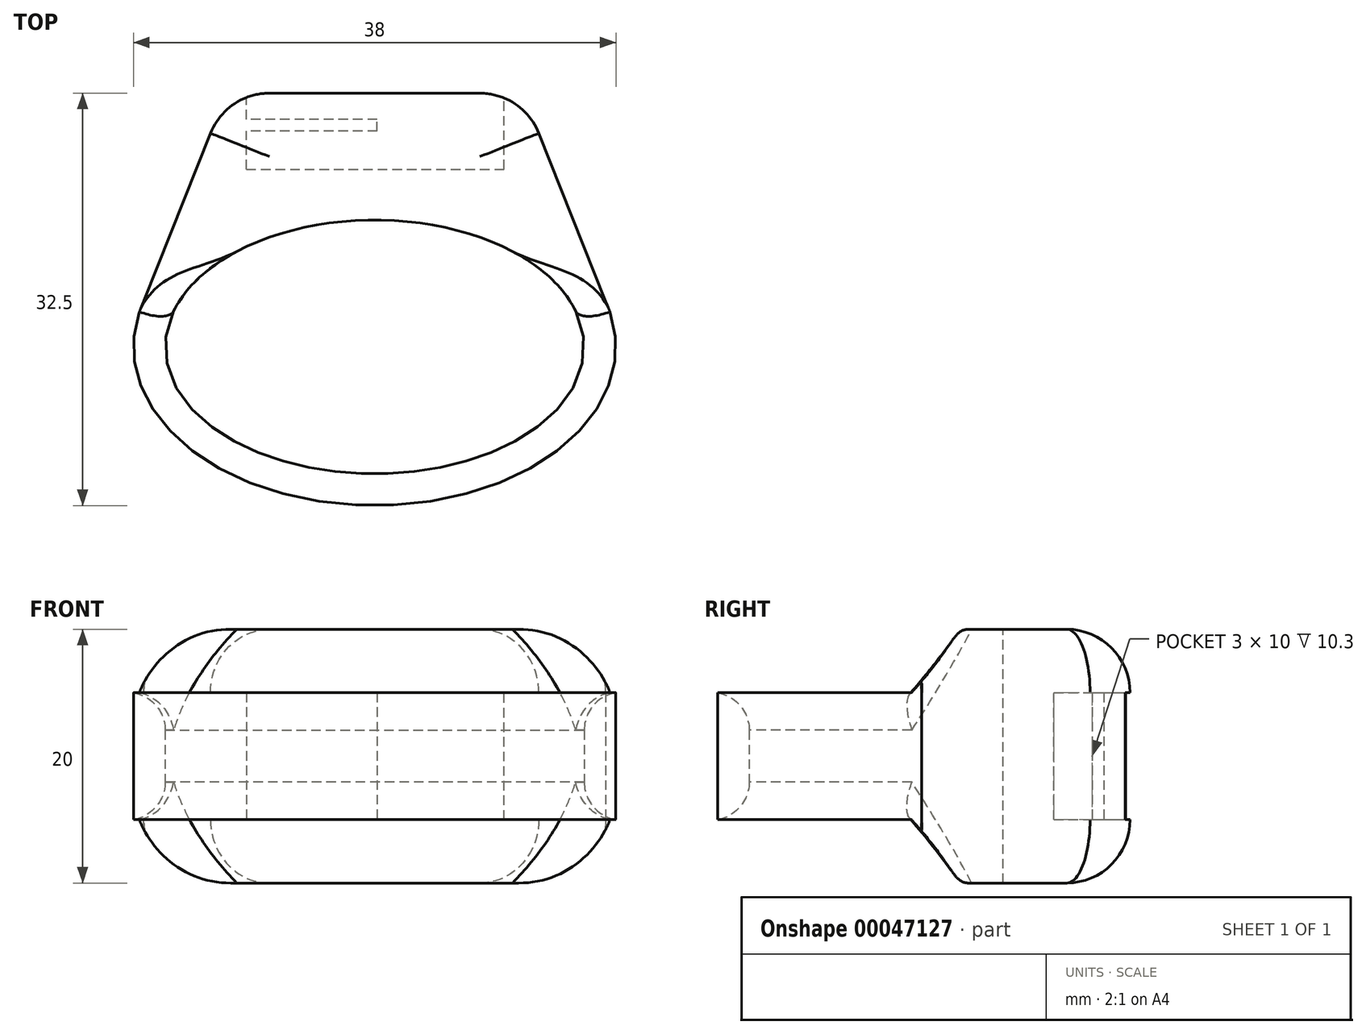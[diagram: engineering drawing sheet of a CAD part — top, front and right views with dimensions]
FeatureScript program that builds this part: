
annotation { "Feature Type Name" : "Feature", "Feature Type Description" : "" }
export const myFeature = defineFeature(function(context is Context, id is Id, definition is map)
    precondition{}
    {
        {
            var Q0;
            Q0=qCreatedBy(makeId("Top.planeOp"),FACE);
            var sketch = newSketch(context, id + "F0", { "sketchPlane" : qUnion([Q0])});
            skEllipse(sketch, "E0", {"center": v(0, 0) * mm, "majorRadius": 16.5 * mm, "minorRadius": 10 * mm, "majorAxis": v(1, 0)});
            skEllipse(sketch, "E1", {"center": v(0, 0) * mm, "majorRadius": 19 * mm, "minorRadius": 12.5 * mm, "majorAxis": v(1, 0)});
            skPoint(sketch, "E2.endSnap0", {"position": v(0, 12.5) * mm});
            skLineSegment(sketch, "E3", {"start": v(0, 12.5) * mm, "end": v(0, 27.8) * mm, "construction": true});
            skLineSegment(sketch, "E4", {"start": v(11.67, 20) * mm, "end": v(0, 20) * mm});
            skLineSegment(sketch, "E5.MirrorCS", {"start": v(-11.67, 20) * mm, "end": v(0, 20) * mm});
            skLineSegment(sketch, "E6", {"start": v(0, 10) * mm, "end": v(45.24, 10) * mm, "construction": true});
            skPoint(sketch, "E7.end.orphan", {"position": v(18.92, -1.17) * mm});
            skPoint(sketch, "E8.orphan", {"position": v(-18.92, -1.17) * mm});
            skPoint(sketch, "E9.MirrorCS.start.orphan", {"position": v(-11.67, 20) * mm});
            skLineSegment(sketch, "E10", {"start": v(11.67, 20) * mm, "end": v(18.54, 2.73) * mm});
            skLineSegment(sketch, "E11.MirrorCS", {"start": v(-11.67, 20) * mm, "end": v(-18.54, 2.73) * mm});
            skLineSegment(sketch, "E12", {"start": v(-18.54, 2.73) * mm, "end": v(-16.23, 1.81) * mm});
            skLineSegment(sketch, "E13", {"start": v(18.54, 2.73) * mm, "end": v(16.23, 1.81) * mm});
            skSolve(sketch);
        }
        {
            var Q0;
            {var subQ0=sQuery(id+"F0.wireOp",EDGE,"E10");var subQ1=sQuery(id+"F0.wireOp",EDGE,"E1");var subQ3=makeQuery(id+"F0.imprint","INTERSECT",VERTEX,{"derivedFrom":[subQ1,subQ0]});Q0=makeQuery(id+"F0.imprint","IMPRINT",FACE,{"disambiguationData":[TD([[makeQuery(id+"F0.imprint","IMPRINT",EDGE,{"disambiguationData":[TD([[subQ3,1.0]])],"derivedFrom":subQ1}),1.0]])]});}
            var Q1;
            {var subQ2=sQuery(id+"F0.wireOp",EDGE,"E4");Q1=makeQuery(id+"F0.imprint","IMPRINT",FACE,{"disambiguationData":[TD([[makeQuery(id+"F0.imprint","IMPRINT",EDGE,{"derivedFrom":subQ2}),1.0]])]});}
            var Q2;
            {var subQ0=sQuery(id+"F0.wireOp",EDGE,"E11.MirrorCS");var subQ1=sQuery(id+"F0.wireOp",EDGE,"E1");var subQ3=makeQuery(id+"F0.imprint","INTERSECT",VERTEX,{"derivedFrom":[subQ1,subQ0]});Q2=makeQuery(id+"F0.imprint","IMPRINT",FACE,{"disambiguationData":[TD([[makeQuery(id+"F0.imprint","IMPRINT",EDGE,{"disambiguationData":[TD([[subQ3,-1.0]])],"derivedFrom":subQ1}),1.0]])]});}
            var Q3;
            {var subQ0=sQuery(id+"F0.wireOp",EDGE,"E12");Q3=makeQuery(id+"F0.imprint","IMPRINT",FACE,{"disambiguationData":[TD([[makeQuery(id+"F0.imprint","IMPRINT",EDGE,{"derivedFrom":subQ0}),1.0]])]});}
            extrude(context, id + "F1", {"entities" : qUnion([Q0, Q1, Q2, Q3]), "endBound" : BoundingType.SYMMETRIC, "depth" : 20 * mm});
        }
        {
            var Q0;
            Q0 = qSketchRegion(id + "F0", true);
            extrude(context, id + "F2", {"entities" : qUnion([Q0]), "operationType" : NewBodyOperationType.ADD, "endBound" : BoundingType.SYMMETRIC, "depth" : 10 * mm});
        }
        {
            var Q0;
            Q0=makeQuery(id+"F1.opExtrude","CAP_EDGE",EDGE,{"disambiguationData":[OSD([sQuery(id+"F0.wireOp",EDGE,"E12")])],"isStart":true});
            var Q1;
            Q1=makeQuery(id+"F1.opExtrude","CAP_EDGE",EDGE,{"disambiguationData":[OSD([sQuery(id+"F0.wireOp",EDGE,"E12")])],"isStart":false});
            var Q2;
            Q2=makeQuery(id+"F1.opExtrude","CAP_EDGE",EDGE,{"disambiguationData":[OSD([sQuery(id+"F0.wireOp",EDGE,"E13")])],"isStart":false});
            var Q3;
            Q3=makeQuery(id+"F1.opExtrude","CAP_EDGE",EDGE,{"disambiguationData":[OSD([sQuery(id+"F0.wireOp",EDGE,"E13")])],"isStart":true});
            chamfer(context, id + "F3", {"entities" : qUnion([Q0, Q1, Q2, Q3]), "width" : 5 * mm, "tangentPropagation" : true});
        }
        {
            var Q0;
            Q0=makeQuery(id+"F2.opExtrude","CAP_EDGE",EDGE,{"disambiguationData":[OSD([sQuery(id+"F0.wireOp",EDGE,"E0")])],"isStart":false});
            var Q1;
            Q1=makeQuery(id+"F2.opExtrude","CAP_EDGE",EDGE,{"disambiguationData":[OSD([sQuery(id+"F0.wireOp",EDGE,"E0")])],"isStart":true});
            var Q2;
            {var subQ0=sQuery(id+"F0.wireOp",EDGE,"E0");Q2=makeQuery(id+"F3.opChamfer","BLEND_EDGE",EDGE,{"blendedFrom":[makeQuery(id+"F1.opExtrude","CAP_EDGE",EDGE,{"disambiguationData":[OSD([sQuery(id+"F0.wireOp",EDGE,"E12")])],"isStart":false}),makeQuery(id+"F2.boolean.opBoolean","MERGE",FACE,{"derivedFrom":[makeQuery(id+"F1.opExtrude","SWEPT_FACE",FACE,{"disambiguationData":[OSD([subQ0])]}),makeQuery(id+"F2.opExtrude","SWEPT_FACE",FACE,{"disambiguationData":[OSD([subQ0])]})]})],"blendedInto":[makeQuery(id+"F2.boolean.opBoolean","MERGE",FACE,{"derivedFrom":[makeQuery(id+"F1.opExtrude","SWEPT_FACE",FACE,{"disambiguationData":[OSD([subQ0])]}),makeQuery(id+"F2.opExtrude","SWEPT_FACE",FACE,{"disambiguationData":[OSD([subQ0])]})]})]});}
            var Q3;
            {var subQ0=sQuery(id+"F0.wireOp",EDGE,"E0");Q3=makeQuery(id+"F3.opChamfer","BLEND_EDGE",EDGE,{"blendedFrom":[makeQuery(id+"F1.opExtrude","CAP_EDGE",EDGE,{"disambiguationData":[OSD([sQuery(id+"F0.wireOp",EDGE,"E13")])],"isStart":false}),makeQuery(id+"F2.boolean.opBoolean","MERGE",FACE,{"derivedFrom":[makeQuery(id+"F1.opExtrude","SWEPT_FACE",FACE,{"disambiguationData":[OSD([subQ0])]}),makeQuery(id+"F2.opExtrude","SWEPT_FACE",FACE,{"disambiguationData":[OSD([subQ0])]})]})],"blendedInto":[makeQuery(id+"F2.boolean.opBoolean","MERGE",FACE,{"derivedFrom":[makeQuery(id+"F1.opExtrude","SWEPT_FACE",FACE,{"disambiguationData":[OSD([subQ0])]}),makeQuery(id+"F2.opExtrude","SWEPT_FACE",FACE,{"disambiguationData":[OSD([subQ0])]})]})]});}
            var Q4;
            {var subQ0=sQuery(id+"F0.wireOp",EDGE,"E0");Q4=makeQuery(id+"F3.opChamfer","BLEND_EDGE",EDGE,{"blendedFrom":[makeQuery(id+"F1.opExtrude","CAP_EDGE",EDGE,{"disambiguationData":[OSD([sQuery(id+"F0.wireOp",EDGE,"E12")])],"isStart":true}),makeQuery(id+"F2.boolean.opBoolean","MERGE",FACE,{"derivedFrom":[makeQuery(id+"F1.opExtrude","SWEPT_FACE",FACE,{"disambiguationData":[OSD([subQ0])]}),makeQuery(id+"F2.opExtrude","SWEPT_FACE",FACE,{"disambiguationData":[OSD([subQ0])]})]})],"blendedInto":[makeQuery(id+"F2.boolean.opBoolean","MERGE",FACE,{"derivedFrom":[makeQuery(id+"F1.opExtrude","SWEPT_FACE",FACE,{"disambiguationData":[OSD([subQ0])]}),makeQuery(id+"F2.opExtrude","SWEPT_FACE",FACE,{"disambiguationData":[OSD([subQ0])]})]})]});}
            var Q5;
            {var subQ0=sQuery(id+"F0.wireOp",EDGE,"E0");Q5=makeQuery(id+"F3.opChamfer","BLEND_EDGE",EDGE,{"blendedFrom":[makeQuery(id+"F1.opExtrude","CAP_EDGE",EDGE,{"disambiguationData":[OSD([sQuery(id+"F0.wireOp",EDGE,"E13")])],"isStart":true}),makeQuery(id+"F2.boolean.opBoolean","MERGE",FACE,{"derivedFrom":[makeQuery(id+"F1.opExtrude","SWEPT_FACE",FACE,{"disambiguationData":[OSD([subQ0])]}),makeQuery(id+"F2.opExtrude","SWEPT_FACE",FACE,{"disambiguationData":[OSD([subQ0])]})]})],"blendedInto":[makeQuery(id+"F2.boolean.opBoolean","MERGE",FACE,{"derivedFrom":[makeQuery(id+"F1.opExtrude","SWEPT_FACE",FACE,{"disambiguationData":[OSD([subQ0])]}),makeQuery(id+"F2.opExtrude","SWEPT_FACE",FACE,{"disambiguationData":[OSD([subQ0])]})]})]});}
            fillet(context, id + "F4", {"entities" : qUnion([Q0, Q1, Q2, Q3, Q4, Q5]), "radius" : 3 * mm, "tangentPropagation" : true, "allowEdgeOverflow" : false});
        }
        {
            var Q0;
            Q0=makeQuery(id+"F1.opExtrude","CAP_EDGE",EDGE,{"disambiguationData":[OSD([sQuery(id+"F0.wireOp",EDGE,"E10")])],"isStart":true});
            var Q1;
            Q1=makeQuery(id+"F1.opExtrude","CAP_EDGE",EDGE,{"disambiguationData":[OSD([sQuery(id+"F0.wireOp",EDGE,"E10")])],"isStart":false});
            var Q2;
            Q2=makeQuery(id+"F1.opExtrude","CAP_EDGE",EDGE,{"disambiguationData":[OSD([sQuery(id+"F0.wireOp",EDGE,"E11.MirrorCS")])],"isStart":true});
            var Q3;
            Q3=makeQuery(id+"F1.opExtrude","CAP_EDGE",EDGE,{"disambiguationData":[OSD([sQuery(id+"F0.wireOp",EDGE,"E11.MirrorCS")])],"isStart":false});
            fillet(context, id + "F5", {"entities" : qUnion([Q0, Q1, Q2, Q3]), "radius" : 5 * mm, "tangentPropagation" : true, "allowEdgeOverflow" : false});
        }
        {
            var Q0;
            Q0=makeQuery(id+"F1.opExtrude","SWEPT_FACE",FACE,{"disambiguationData":[OSD([sQuery(id+"F0.wireOp",EDGE,"E4"),sQuery(id+"F0.wireOp",EDGE,"E5.MirrorCS")])]});
            var sketch = newSketch(context, id + "F6", { "sketchPlane" : qUnion([Q0])});
            skPoint(sketch, "E14.oppositeSnap0", {"position": v(0.91, 5) * mm});
            skLineSegment(sketch, "E14.bottom", {"start": v(10.1, -5) * mm, "end": v(-10.17, -5) * mm});
            skLineSegment(sketch, "E14.top", {"start": v(10.1, 5) * mm, "end": v(-10.17, 5) * mm});
            skLineSegment(sketch, "E14.left", {"start": v(10.1, -5) * mm, "end": v(10.1, 5) * mm});
            skLineSegment(sketch, "E14.right", {"start": v(-10.17, -5) * mm, "end": v(-10.17, 5) * mm});
            skSolve(sketch);
        }
        {
            var Q0;
            Q0 = qSketchRegion(id + "F6", true);
            extrude(context, id + "F7", {"entities" : qUnion([Q0]), "operationType" : NewBodyOperationType.REMOVE, "oppositeDirection" : true, "depth" : 6 * mm});
        }
        {
            var Q0;
            Q0=makeQuery(id+"F7.boolean.opBoolean","COPY",FACE,{"derivedFrom":makeQuery(id+"F7.opExtrude","SWEPT_FACE",FACE,{"disambiguationData":[OSD([sQuery(id+"F6.wireOp",EDGE,"E14.left")])]})});
            var sketch = newSketch(context, id + "F8", { "sketchPlane" : qUnion([Q0])});
            skLineSegment(sketch, "E15.bottom", {"start": v(17.93, 5) * mm, "end": v(17, 5) * mm});
            skLineSegment(sketch, "E15.top", {"start": v(17.93, -5) * mm, "end": v(17, -5) * mm});
            skLineSegment(sketch, "E15.left", {"start": v(17, 5) * mm, "end": v(17, -5) * mm});
            skLineSegment(sketch, "E15.right", {"start": v(17.93, 5) * mm, "end": v(17.93, -5) * mm});
            skSolve(sketch);
        }
        {
            var Q0;
            Q0 = qSketchRegion(id + "F8", true);
            extrude(context, id + "F9", {"entities" : qUnion([Q0]), "operationType" : NewBodyOperationType.ADD, "depth" : 10.3 * mm});
        }
        {
            var Q0;
            Q0=makeQuery(id+"F1.opExtrude","CAP_EDGE",EDGE,{"disambiguationData":[OSD([sQuery(id+"F0.wireOp",EDGE,"E4"),sQuery(id+"F0.wireOp",EDGE,"E5.MirrorCS")])],"isStart":false});
            var Q1;
            Q1=makeQuery(id+"F5.opFillet","BLEND_EDGE",EDGE,{"blendedFrom":[makeQuery(id+"F1.opExtrude","CAP_EDGE",EDGE,{"disambiguationData":[OSD([sQuery(id+"F0.wireOp",EDGE,"E10")])],"isStart":false}),makeQuery(id+"F1.opExtrude","SWEPT_FACE",FACE,{"disambiguationData":[OSD([sQuery(id+"F0.wireOp",EDGE,"E4"),sQuery(id+"F0.wireOp",EDGE,"E5.MirrorCS")])]})],"blendedInto":[makeQuery(id+"F1.opExtrude","SWEPT_FACE",FACE,{"disambiguationData":[OSD([sQuery(id+"F0.wireOp",EDGE,"E4"),sQuery(id+"F0.wireOp",EDGE,"E5.MirrorCS")])]})]});
            var Q2;
            Q2=makeQuery(id+"F1.opExtrude","SWEPT_EDGE",EDGE,{"disambiguationData":[OSD([sQuery(id+"F0.wireOp",EDGE,"E4"),sQuery(id+"F0.wireOp",EDGE,"E10")])]});
            var Q3;
            Q3=makeQuery(id+"F5.opFillet","BLEND_EDGE",EDGE,{"blendedFrom":[makeQuery(id+"F1.opExtrude","CAP_EDGE",EDGE,{"disambiguationData":[OSD([sQuery(id+"F0.wireOp",EDGE,"E10")])],"isStart":true}),makeQuery(id+"F1.opExtrude","SWEPT_FACE",FACE,{"disambiguationData":[OSD([sQuery(id+"F0.wireOp",EDGE,"E4"),sQuery(id+"F0.wireOp",EDGE,"E5.MirrorCS")])]})],"blendedInto":[makeQuery(id+"F1.opExtrude","SWEPT_FACE",FACE,{"disambiguationData":[OSD([sQuery(id+"F0.wireOp",EDGE,"E4"),sQuery(id+"F0.wireOp",EDGE,"E5.MirrorCS")])]})]});
            var Q4;
            Q4=makeQuery(id+"F1.opExtrude","CAP_EDGE",EDGE,{"disambiguationData":[OSD([sQuery(id+"F0.wireOp",EDGE,"E4"),sQuery(id+"F0.wireOp",EDGE,"E5.MirrorCS")])],"isStart":true});
            var Q5;
            Q5=makeQuery(id+"F5.opFillet","BLEND_EDGE",EDGE,{"blendedFrom":[makeQuery(id+"F1.opExtrude","CAP_EDGE",EDGE,{"disambiguationData":[OSD([sQuery(id+"F0.wireOp",EDGE,"E11.MirrorCS")])],"isStart":true}),makeQuery(id+"F1.opExtrude","SWEPT_FACE",FACE,{"disambiguationData":[OSD([sQuery(id+"F0.wireOp",EDGE,"E4"),sQuery(id+"F0.wireOp",EDGE,"E5.MirrorCS")])]})],"blendedInto":[makeQuery(id+"F1.opExtrude","SWEPT_FACE",FACE,{"disambiguationData":[OSD([sQuery(id+"F0.wireOp",EDGE,"E4"),sQuery(id+"F0.wireOp",EDGE,"E5.MirrorCS")])]})]});
            var Q6;
            Q6=makeQuery(id+"F1.opExtrude","SWEPT_EDGE",EDGE,{"disambiguationData":[OSD([sQuery(id+"F0.wireOp",EDGE,"E5.MirrorCS"),sQuery(id+"F0.wireOp",EDGE,"E11.MirrorCS")])]});
            var Q7;
            Q7=makeQuery(id+"F5.opFillet","BLEND_EDGE",EDGE,{"blendedFrom":[makeQuery(id+"F1.opExtrude","CAP_EDGE",EDGE,{"disambiguationData":[OSD([sQuery(id+"F0.wireOp",EDGE,"E11.MirrorCS")])],"isStart":false}),makeQuery(id+"F1.opExtrude","SWEPT_FACE",FACE,{"disambiguationData":[OSD([sQuery(id+"F0.wireOp",EDGE,"E4"),sQuery(id+"F0.wireOp",EDGE,"E5.MirrorCS")])]})],"blendedInto":[makeQuery(id+"F1.opExtrude","SWEPT_FACE",FACE,{"disambiguationData":[OSD([sQuery(id+"F0.wireOp",EDGE,"E4"),sQuery(id+"F0.wireOp",EDGE,"E5.MirrorCS")])]})]});
            fillet(context, id + "F10", {"entities" : qUnion([Q0, Q1, Q2, Q3, Q4, Q5, Q6, Q7]), "radius" : 5 * mm, "tangentPropagation" : true, "allowEdgeOverflow" : false});
        }
    });
